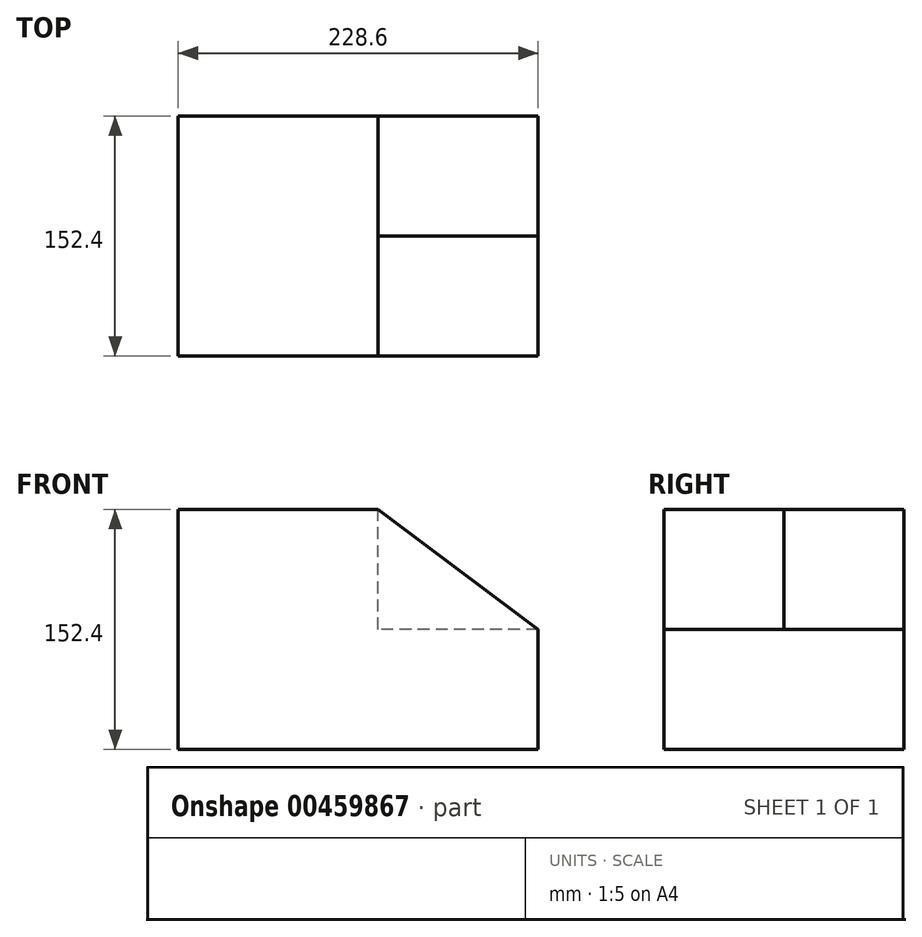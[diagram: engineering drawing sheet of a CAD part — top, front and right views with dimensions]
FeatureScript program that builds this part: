
annotation { "Feature Type Name" : "Feature", "Feature Type Description" : "" }
export const myFeature = defineFeature(function(context is Context, id is Id, definition is map)
    precondition{}
    {
        {
            var Q0;
            Q0=qCreatedBy(makeId("Front.planeOp"),FACE);
            var sketch = newSketch(context, id + "F0", { "sketchPlane" : qUnion([Q0])});
            skLineSegment(sketch, "E0", {"start": v(0, 0) * mm, "end": v(-228.6, 0) * mm});
            skLineSegment(sketch, "E1", {"start": v(-228.6, 0) * mm, "end": v(-228.6, 152.4) * mm});
            skLineSegment(sketch, "E2", {"start": v(-228.6, 152.4) * mm, "end": v(-101.6, 152.4) * mm});
            skLineSegment(sketch, "E3", {"start": v(-101.6, 152.4) * mm, "end": v(0, 76.2) * mm});
            skLineSegment(sketch, "E4", {"start": v(0, 76.2) * mm, "end": v(0, 0) * mm});
            skSolve(sketch);
        }
        {
            var Q0;
            Q0=makeQuery(id+"F0.imprint","IMPRINT",FACE,{"disambiguationData":[TD([[makeQuery(id+"F0.imprint","IMPRINT",EDGE,{"derivedFrom":sQuery(id+"F0.wireOp",EDGE,"E0")}),-1.0]])]});
            extrude(context, id + "F1", {"entities" : qUnion([Q0]), "depth" : 152.4 * mm});
        }
        {
            var Q0;
            Q0=makeQuery(id+"F1.opExtrude","CAP_FACE",FACE,{"disambiguationData":[OSD([sQuery(id+"F0.wireOp",EDGE,"E0"),sQuery(id+"F0.wireOp",EDGE,"E1"),sQuery(id+"F0.wireOp",EDGE,"E2"),sQuery(id+"F0.wireOp",EDGE,"E3"),sQuery(id+"F0.wireOp",EDGE,"E4")])],"isStart":true});
            var sketch = newSketch(context, id + "F2", { "sketchPlane" : qUnion([Q0])});
            skLineSegment(sketch, "E5", {"start": v(0, 76.2) * mm, "end": v(101.6, 76.2) * mm});
            skLineSegment(sketch, "E6", {"start": v(101.6, 76.2) * mm, "end": v(101.6, 152.4) * mm});
            skSolve(sketch);
        }
        {
            var Q0;
            Q0=makeQuery(id+"F2.imprint","IMPRINT",FACE,{"disambiguationData":[TD([[makeQuery(id+"F2.imprint","IMPRINT",EDGE,{"derivedFrom":sQuery(id+"F2.wireOp",EDGE,"E5")}),1.0]])]});
            extrude(context, id + "F3", {"entities" : qUnion([Q0]), "operationType" : NewBodyOperationType.REMOVE, "oppositeDirection" : true, "depth" : 76.2 * mm});
        }
    });
